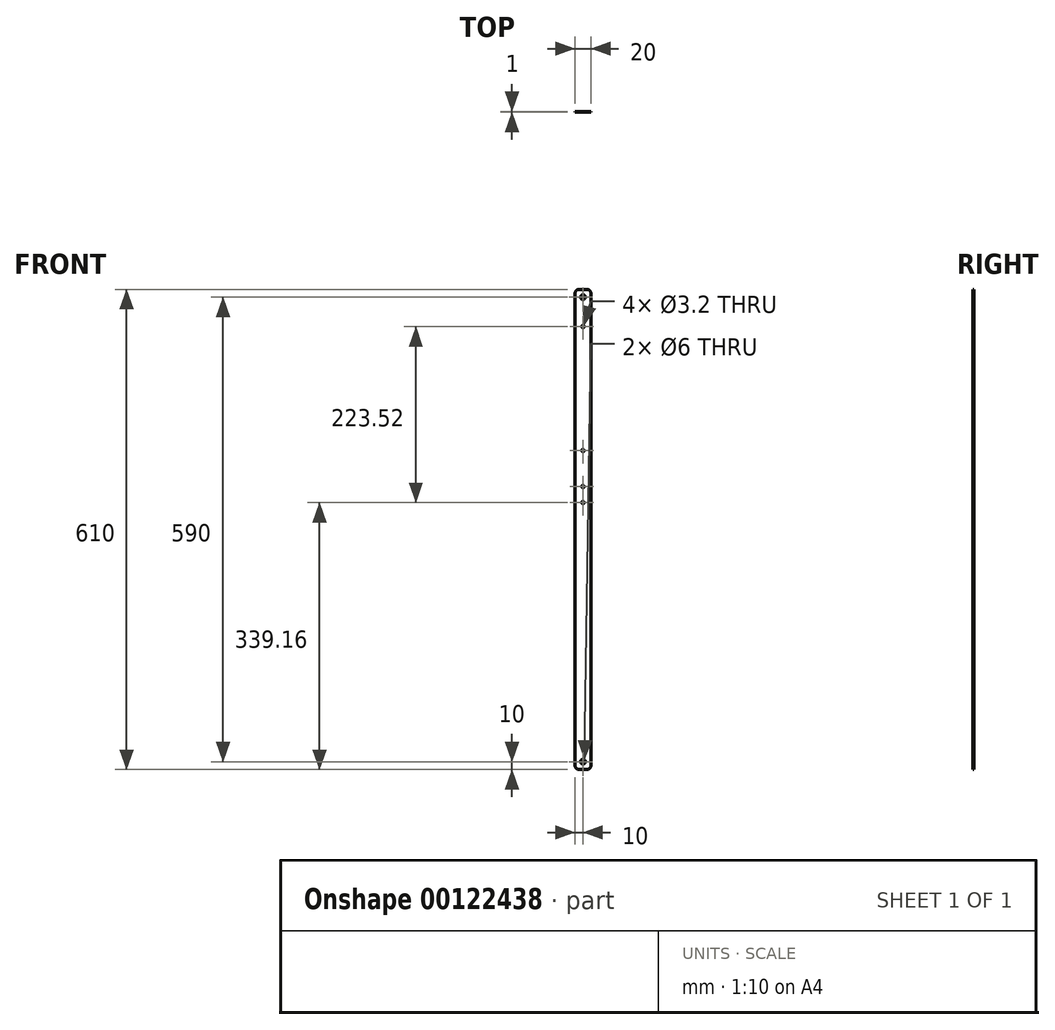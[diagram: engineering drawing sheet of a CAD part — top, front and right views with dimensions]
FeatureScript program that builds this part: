
annotation { "Feature Type Name" : "Feature", "Feature Type Description" : "" }
export const myFeature = defineFeature(function(context is Context, id is Id, definition is map)
    precondition{}
    {
        {
            var Q0;
            Q0=qCreatedBy(makeId("Front.planeOp"),FACE);
            var sketch = newSketch(context, id + "F0", { "sketchPlane" : qUnion([Q0])});
            skLineSegment(sketch, "E0.bottom", {"start": v(5, 0) * mm, "end": v(15, 0) * mm});
            skLineSegment(sketch, "E0.top", {"start": v(5, 610) * mm, "end": v(15, 610) * mm});
            skLineSegment(sketch, "E0.left", {"start": v(0, 5) * mm, "end": v(0, 605) * mm});
            skLineSegment(sketch, "E0.right", {"start": v(20, 5) * mm, "end": v(20, 605) * mm});
            skCircle(sketch, "E1", {"center": v(10, 10) * mm, "radius": 3 * mm});
            skPoint(sketch, "E1.centerSnap0", {"position": v(10, 0) * mm});
            skCircle(sketch, "E2", {"center": v(10, 600) * mm, "radius": 3 * mm});
            skPoint(sketch, "E2.centerSnap0", {"position": v(10, 610) * mm});
            skCircle(sketch, "E3", {"center": v(10, 562.68) * mm, "radius": 1.6 * mm});
            skCircle(sketch, "E4", {"center": v(10, 405.2) * mm, "radius": 1.6 * mm});
            skCircle(sketch, "E5", {"center": v(10, 359.48) * mm, "radius": 1.6 * mm});
            skCircle(sketch, "E6", {"center": v(10, 339.16) * mm, "radius": 1.6 * mm});
            skPoint(sketch, "E7.visualSharp", {"position": v(0, 610) * mm});
            skArc(sketch, "E7.filletArc", {"start": v(5, 610) * mm, "mid": v(1.46, 608.54) * mm, "end": v(0, 605) * mm});
            skPoint(sketch, "E8.visualSharp", {"position": v(20, 610) * mm});
            skArc(sketch, "E8.filletArc", {"start": v(20, 605) * mm, "mid": v(18.54, 608.54) * mm, "end": v(15, 610) * mm});
            skPoint(sketch, "E9.visualSharp", {"position": v(0, 0) * mm});
            skArc(sketch, "E9.filletArc", {"start": v(0, 5) * mm, "mid": v(1.46, 1.46) * mm, "end": v(5, 0) * mm});
            skPoint(sketch, "E10.visualSharp", {"position": v(20, 0) * mm});
            skArc(sketch, "E10.filletArc", {"start": v(15, 0) * mm, "mid": v(18.54, 1.46) * mm, "end": v(20, 5) * mm});
            skSolve(sketch);
        }
        {
            var Q0;
            Q0 = qSketchRegion(id + "F0", true);
            extrude(context, id + "F1", {"entities" : qUnion([Q0]), "depth" : 1 * mm});
        }
    });
